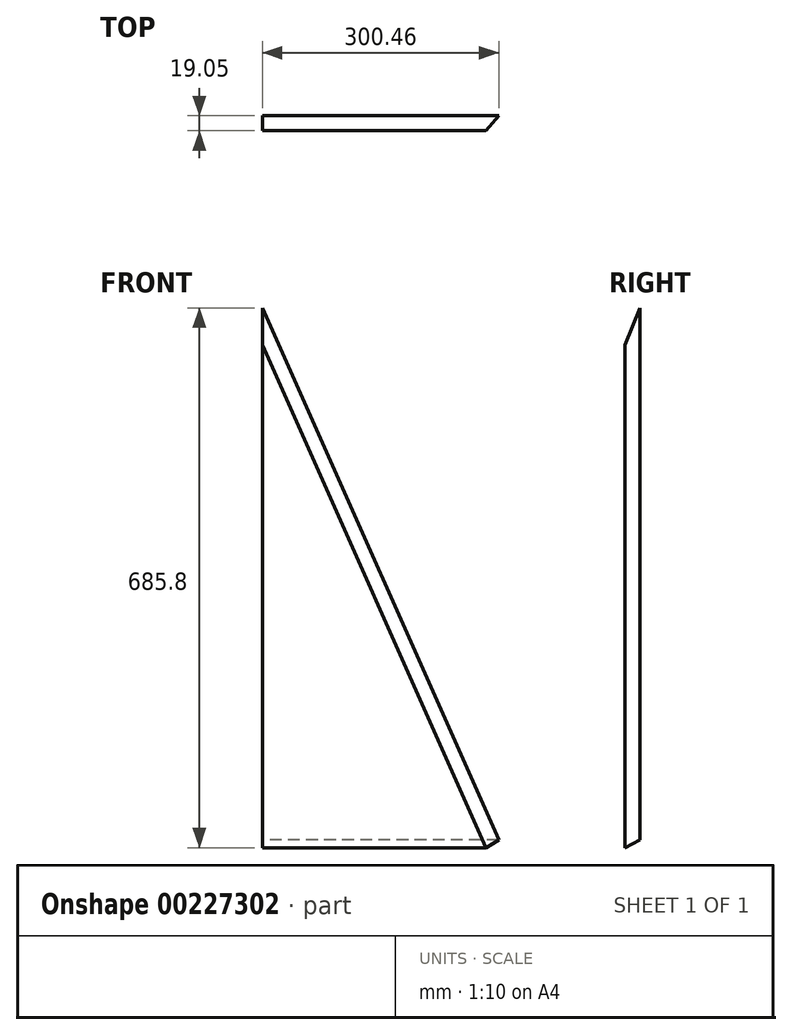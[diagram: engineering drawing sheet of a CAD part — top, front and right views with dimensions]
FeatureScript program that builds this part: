
annotation { "Feature Type Name" : "Feature", "Feature Type Description" : "" }
export const myFeature = defineFeature(function(context is Context, id is Id, definition is map)
    precondition{}
    {
        {
            var Q0;
            Q0=qCreatedBy(makeId("Front.planeOp"),FACE);
            var sketch = newSketch(context, id + "F0", { "sketchPlane" : qUnion([Q0])});
            skLineSegment(sketch, "E0.top", {"start": v(-205.98, -389.33) * mm, "end": v(98.82, -389.33) * mm});
            skLineSegment(sketch, "E0.left", {"start": v(-205.98, 296.47) * mm, "end": v(-205.98, -389.33) * mm});
            skLineSegment(sketch, "E1", {"start": v(-205.98, 296.47) * mm, "end": v(98.82, -389.33) * mm});
            skSolve(sketch);
        }
        {
            var Q0;
            Q0=makeQuery(id+"F0.imprint","IMPRINT",FACE,{"disambiguationData":[TD([[makeQuery(id+"F0.imprint","IMPRINT",EDGE,{"derivedFrom":sQuery(id+"F0.wireOp",EDGE,"E0.top")}),1.0]])]});
            extrude(context, id + "F1", {"entities" : qUnion([Q0]), "depth" : 19.05 * mm});
        }
        {
            var Q0;
            Q0=makeQuery(id+"F1.opExtrude","CAP_EDGE",EDGE,{"disambiguationData":[OSD([sQuery(id+"F0.wireOp",EDGE,"E0.top")])],"isStart":true});
            chamfer(context, id + "F2", {"entities" : qUnion([Q0]), "chamferType" : ChamferType.OFFSET_ANGLE, "width" : 19.05 * mm, "oppositeDirection" : false, "angle" : 27.14 * degree, "tangentPropagation" : true});
        }
        {
            var Q0;
            Q0=makeQuery(id+"F1.opExtrude","CAP_EDGE",EDGE,{"disambiguationData":[OSD([sQuery(id+"F0.wireOp",EDGE,"E1")])],"isStart":false});
            chamfer(context, id + "F3", {"entities" : qUnion([Q0]), "chamferType" : ChamferType.OFFSET_ANGLE, "width" : 19.05 * mm, "oppositeDirection" : true, "angle" : 45 * degree, "tangentPropagation" : true});
        }
    });
